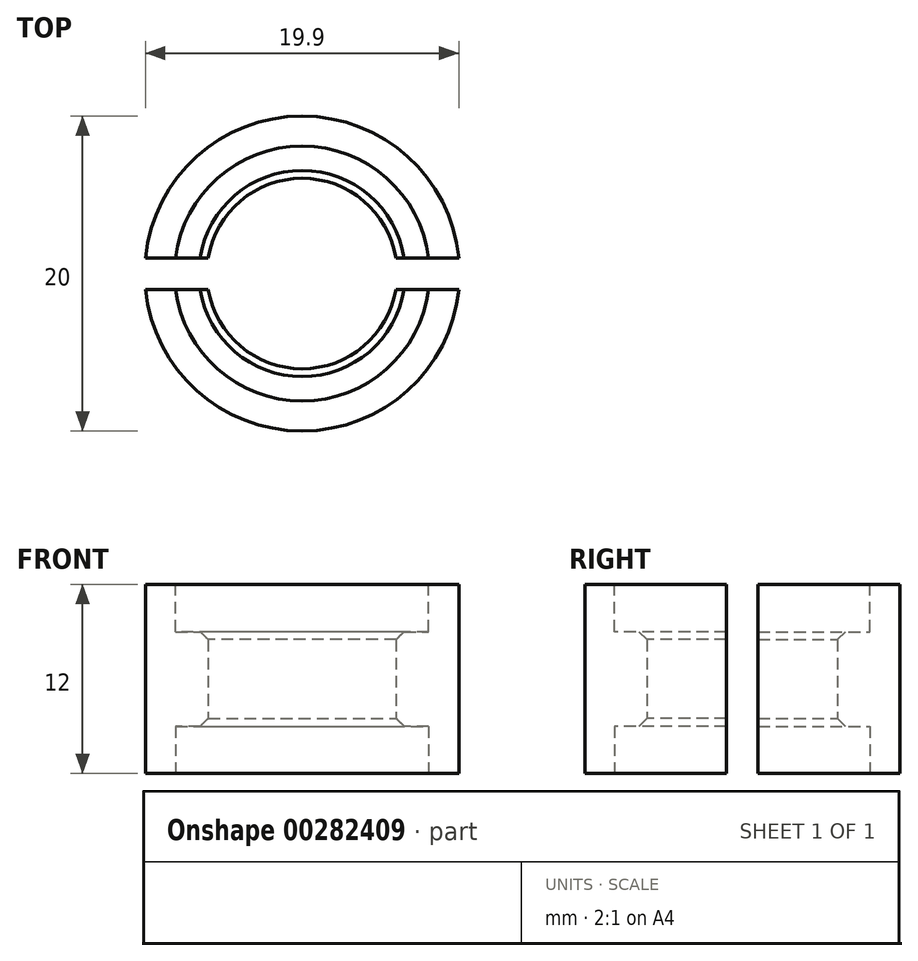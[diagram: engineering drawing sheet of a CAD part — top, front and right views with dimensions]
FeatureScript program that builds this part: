
annotation { "Feature Type Name" : "Feature", "Feature Type Description" : "" }
export const myFeature = defineFeature(function(context is Context, id is Id, definition is map)
    precondition{}
    {
        {
            var Q0;
            Q0=qCreatedBy(makeId("Top.planeOp"),FACE);
            var sketch = newSketch(context, id + "F0", { "sketchPlane" : qUnion([Q0])});
            skCircle(sketch, "E0", {"center": v(0, 0) * mm, "radius": 10 * mm});
            skCircle(sketch, "E1", {"center": v(0, 0) * mm, "radius": 6.05 * mm});
            skSolve(sketch);
        }
        {
            var Q0;
            Q0=qSketchRegion(id+"F0",true);
            extrude(context, id + "F1", {"entities" : qUnion([Q0]), "depth" : 12 * mm});
        }
        {
            var Q0;
            Q0=makeQuery(id+"F1.opExtrude","CAP_FACE",FACE,{"disambiguationData":[OSD([sQuery(id+"F0.wireOp",EDGE,"E0"),sQuery(id+"F0.wireOp",EDGE,"E1")])],"isStart":false});
            var sketch = newSketch(context, id + "F2", { "sketchPlane" : qUnion([Q0])});
            skCircle(sketch, "E2", {"center": v(0, 0) * mm, "radius": 8.1 * mm});
            skSolve(sketch);
        }
        {
            var Q0;
            Q0=qSketchRegion(id+"F2",true);
            extrude(context, id + "F3", {"entities" : qUnion([Q0]), "operationType" : NewBodyOperationType.REMOVE, "oppositeDirection" : true, "depth" : 3 * mm});
        }
        {
            var Q0;
            Q0=makeQuery(id+"F1.opExtrude","CAP_FACE",FACE,{"disambiguationData":[OSD([sQuery(id+"F0.wireOp",EDGE,"E0"),sQuery(id+"F0.wireOp",EDGE,"E1")])],"isStart":true});
            var sketch = newSketch(context, id + "F4", { "sketchPlane" : qUnion([Q0])});
            skCircle(sketch, "E3", {"center": v(0, 0) * mm, "radius": 8.1 * mm});
            skSolve(sketch);
        }
        {
            var Q0;
            Q0=qSketchRegion(id+"F4",true);
            extrude(context, id + "F5", {"entities" : qUnion([Q0]), "operationType" : NewBodyOperationType.REMOVE, "oppositeDirection" : true, "depth" : 3 * mm});
        }
        {
            var Q0;
            Q0=makeQuery(id+"F5.boolean.opBoolean","INTERSECT",EDGE,{"derivedFrom":[makeQuery(id+"F1.opExtrude","SWEPT_FACE",FACE,{"disambiguationData":[OSD([sQuery(id+"F0.wireOp",EDGE,"E1")])]}),makeQuery(id+"F5.opExtrude","CAP_FACE",FACE,{"disambiguationData":[OSD([sQuery(id+"F4.wireOp",EDGE,"E3")])],"isStart":false})]});
            var Q1;
            Q1=makeQuery(id+"F3.boolean.opBoolean","INTERSECT",EDGE,{"derivedFrom":[makeQuery(id+"F1.opExtrude","SWEPT_FACE",FACE,{"disambiguationData":[OSD([sQuery(id+"F0.wireOp",EDGE,"E1")])]}),makeQuery(id+"F3.opExtrude","CAP_FACE",FACE,{"disambiguationData":[OSD([sQuery(id+"F2.wireOp",EDGE,"E2")])],"isStart":false})]});
            chamfer(context, id + "F6", {"entities" : qUnion([Q0, Q1]), "width" : 0.5 * mm, "tangentPropagation" : true});
        }
        {
            var Q0;
            Q0=makeQuery(id+"F1.opExtrude","CAP_FACE",FACE,{"disambiguationData":[OSD([sQuery(id+"F0.wireOp",EDGE,"E0"),sQuery(id+"F0.wireOp",EDGE,"E1")])],"isStart":false});
            var sketch = newSketch(context, id + "F7", { "sketchPlane" : qUnion([Q0])});
            skLineSegment(sketch, "E4.bottom", {"start": v(-12, 1) * mm, "end": v(12, 1) * mm});
            skLineSegment(sketch, "E4.top", {"start": v(-12, -1) * mm, "end": v(12, -1) * mm});
            skLineSegment(sketch, "E4.left", {"start": v(-12, 1) * mm, "end": v(-12, -1) * mm});
            skLineSegment(sketch, "E4.right", {"start": v(12, 1) * mm, "end": v(12, -1) * mm});
            skSolve(sketch);
        }
        {
            var Q0;
            Q0=qSketchRegion(id+"F7",true);
            extrude(context, id + "F8", {"entities" : qUnion([Q0]), "operationType" : NewBodyOperationType.REMOVE, "endBound" : BoundingType.THROUGH_ALL, "oppositeDirection" : true, "depth" : 25 * mm});
        }
    });
